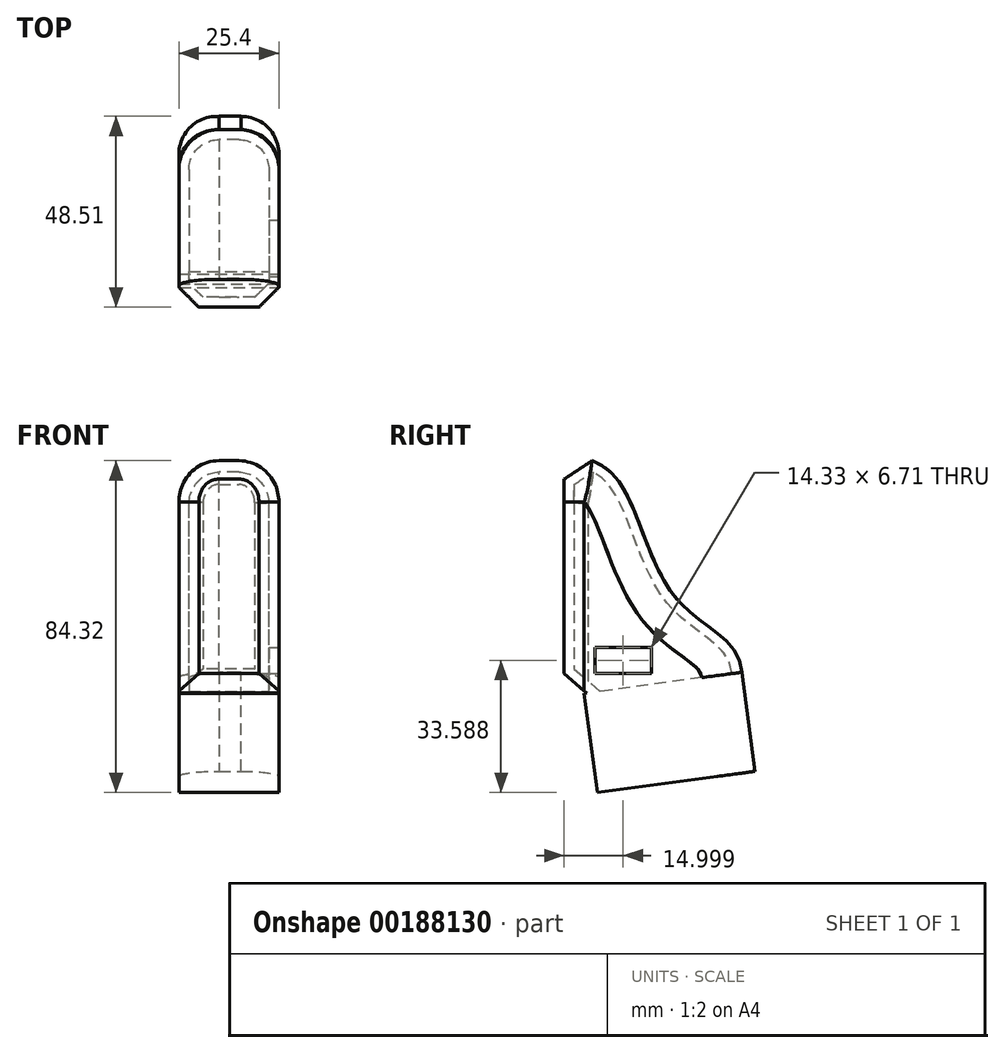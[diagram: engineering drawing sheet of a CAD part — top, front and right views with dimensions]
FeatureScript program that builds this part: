
annotation { "Feature Type Name" : "Feature", "Feature Type Description" : "" }
export const myFeature = defineFeature(function(context is Context, id is Id, definition is map)
    precondition{}
    {
        {
            var Q0;
            Q0=qCreatedBy(makeId("Right.planeOp"),FACE);
            var sketch = newSketch(context, id + "F10", { "sketchPlane" : qUnion([Q0])});
            skFitSpline(sketch, "E0", {"points": [v(0, 43.1) * mm, v(12.97, 36.32) * mm, v(28.4, 5.53) * mm, v(45.1, -13.31) * mm], "startDerivative": vector(44.8, -20.69) * mm, "endDerivative": vector(5.01, -78.47) * mm});
            skLineSegment(sketch, "E1", {"start": v(45.1, -13.31) * mm, "end": v(0, -19.4) * mm});
            skLineSegment(sketch, "E2", {"start": v(0, -19.4) * mm, "end": v(0, 43.1) * mm});
            skSolve(sketch);
        }
        {
            var Q0;
            Q0 = qSketchRegion(id + "F10", true);
            var Q1;
            Q1=makeQuery(id+"F10.imprint","IMPRINT",FACE,{"disambiguationData":[TD([[makeQuery(id+"F10.imprint","IMPRINT",EDGE,{"derivedFrom":sQuery(id+"F10.wireOp",EDGE,"E0")}),-1.0]])]});
            extrude(context, id + "F0", {"entities" : qUnion([Q0, Q1]), "depth" : 12.7 * mm});
        }
        {
            var Q0;
            Q0=makeQuery(id+"F10.imprint","IMPRINT",FACE,{"disambiguationData":[TD([[makeQuery(id+"F10.imprint","IMPRINT",EDGE,{"derivedFrom":sQuery(id+"F10.wireOp",EDGE,"E0")}),-1.0]])]});
            extrude(context, id + "F11", {"entities" : qUnion([Q0]), "operationType" : NewBodyOperationType.ADD, "oppositeDirection" : true, "depth" : 12.7 * mm});
        }
        {
            var Q0;
            Q0=makeQuery(id+"F0.opExtrude","CAP_EDGE",EDGE,{"disambiguationData":[OSD([sQuery(id+"F10.wireOp",EDGE,"E0")])],"isStart":false});
            var Q1;
            Q1=makeQuery(id+"F11.opExtrude","CAP_EDGE",EDGE,{"disambiguationData":[OSD([sQuery(id+"F10.wireOp",EDGE,"E0")])],"isStart":false});
            fillet(context, id + "F1", {"entities" : qUnion([Q0, Q1]), "radius" : 10.16 * mm, "tangentPropagation" : true, "allowEdgeOverflow" : false});
        }
        {
            var Q0;
            {var subQ0=sQuery(id+"F10.wireOp",EDGE,"E2");Q0=makeQuery(id+"F11.boolean.opBoolean","MERGE",FACE,{"derivedFrom":[makeQuery(id+"F0.opExtrude","SWEPT_FACE",FACE,{"disambiguationData":[OSD([subQ0])]}),makeQuery(id+"F11.opExtrude","SWEPT_FACE",FACE,{"disambiguationData":[OSD([subQ0])]})]});}
            chamfer(context, id + "F2", {"entities" : qUnion([Q0]), "width" : 5.08 * mm, "tangentPropagation" : true});
        }
        {
            var Q0;
            {var subQ0=sQuery(id+"F10.wireOp",EDGE,"E1");Q0=makeQuery(id+"F11.boolean.opBoolean","MERGE",FACE,{"derivedFrom":[makeQuery(id+"F0.opExtrude","SWEPT_FACE",FACE,{"disambiguationData":[OSD([subQ0])]}),makeQuery(id+"F11.opExtrude","SWEPT_FACE",FACE,{"disambiguationData":[OSD([subQ0])]})]});}
            shell(context, id + "F3", {"entities" : qUnion([Q0]), "thickness" : 2.54 * mm});
        }
        {
            var Q0;
            {var subQ0=sQuery(id+"F10.wireOp",EDGE,"E1");Q0=makeQuery(id+"F11.boolean.opBoolean","MERGE",FACE,{"derivedFrom":[makeQuery(id+"F0.opExtrude","SWEPT_FACE",FACE,{"disambiguationData":[OSD([subQ0])]}),makeQuery(id+"F11.opExtrude","SWEPT_FACE",FACE,{"disambiguationData":[OSD([subQ0])]})]});}
            var sketch = newSketch(context, id + "F4", { "sketchPlane" : qUnion([Q0])});
            skLineSegment(sketch, "E3", {"start": v(-12.7, -2.48) * mm, "end": v(12.7, -2.48) * mm});
            skLineSegment(sketch, "E4", {"start": v(12.7, -2.48) * mm, "end": v(12.7, -32.73) * mm});
            skLineSegment(sketch, "E5", {"start": v(-12.7, -2.48) * mm, "end": v(-12.7, -32.73) * mm});
            skLineSegment(sketch, "E6", {"start": v(-12.7, -32.73) * mm, "end": v(-12.7, -33.26) * mm});
            skLineSegment(sketch, "E7", {"start": v(-3.05, -42.91) * mm, "end": v(3.05, -42.91) * mm});
            skLineSegment(sketch, "E8", {"start": v(12.7, -33.26) * mm, "end": v(12.7, -32.73) * mm});
            skPoint(sketch, "E9.visualSharp", {"position": v(12.7, -42.91) * mm});
            skArc(sketch, "E9.filletArc", {"start": v(3.05, -42.91) * mm, "mid": v(9.87, -40.09) * mm, "end": v(12.7, -33.26) * mm});
            skPoint(sketch, "E10.visualSharp", {"position": v(-12.7, -42.91) * mm});
            skArc(sketch, "E10.filletArc", {"start": v(-12.7, -33.26) * mm, "mid": v(-9.87, -40.09) * mm, "end": v(-3.05, -42.91) * mm});
            skSolve(sketch);
        }
        {
            var Q0;
            Q0 = qSketchRegion(id + "F4", true);
            extrude(context, id + "F5", {"entities" : qUnion([Q0]), "operationType" : NewBodyOperationType.ADD, "depth" : 25.4 * mm});
        }
        {
            var Q0;
            Q0=makeQuery(id+"F5.boolean.opBoolean","MERGE",FACE,{"derivedFrom":[makeQuery(id+"F0.opExtrude","CAP_FACE",FACE,{"disambiguationData":[OSD([sQuery(id+"F10.wireOp",EDGE,"E0"),sQuery(id+"F10.wireOp",EDGE,"E1"),sQuery(id+"F10.wireOp",EDGE,"E2")])],"isStart":false}),makeQuery(id+"F5.opExtrude","SWEPT_FACE",FACE,{"disambiguationData":[OSD([sQuery(id+"F4.wireOp",EDGE,"E4"),sQuery(id+"F4.wireOp",EDGE,"E8")])]})]});
            var sketch = newSketch(context, id + "F6", { "sketchPlane" : qUnion([Q0])});
            skLineSegment(sketch, "E11.bottom", {"start": v(22.16, -6.95) * mm, "end": v(7.83, -6.95) * mm});
            skLineSegment(sketch, "E11.top", {"start": v(22.16, -13.66) * mm, "end": v(7.83, -13.66) * mm});
            skLineSegment(sketch, "E11.left", {"start": v(22.16, -6.95) * mm, "end": v(22.16, -13.66) * mm});
            skLineSegment(sketch, "E11.right", {"start": v(7.83, -6.95) * mm, "end": v(7.83, -13.66) * mm});
            skSolve(sketch);
        }
        {
            var Q0;
            Q0 = qSketchRegion(id + "F6", true);
            extrude(context, id + "F7", {"entities" : qUnion([Q0]), "operationType" : NewBodyOperationType.REMOVE, "oppositeDirection" : true, "depth" : 2.54 * mm});
        }
        {
            var Q0;
            Q0=makeQuery(id+"F5.opExtrude","SWEPT_FACE",FACE,{"disambiguationData":[OSD([sQuery(id+"F4.wireOp",EDGE,"E7")])]});
            var sketch = newSketch(context, id + "F8", { "sketchPlane" : qUnion([Q0])});
            skLineSegment(sketch, "E12.bottom", {"start": v(2.54, -19.23) * mm, "end": v(-3.05, -19.23) * mm});
            skLineSegment(sketch, "E12.top", {"start": v(2.54, -44.63) * mm, "end": v(-3.05, -44.63) * mm});
            skLineSegment(sketch, "E12.left", {"start": v(2.54, -19.23) * mm, "end": v(2.54, -44.63) * mm});
            skLineSegment(sketch, "E12.right", {"start": v(-3.05, -19.23) * mm, "end": v(-3.05, -44.63) * mm});
            skSolve(sketch);
        }
        {
            var Q0;
            Q0 = qSketchRegion(id + "F8", true);
            extrude(context, id + "F9", {"entities" : qUnion([Q0]), "operationType" : NewBodyOperationType.ADD, "depth" : 0.01 * mm});
        }
    });
